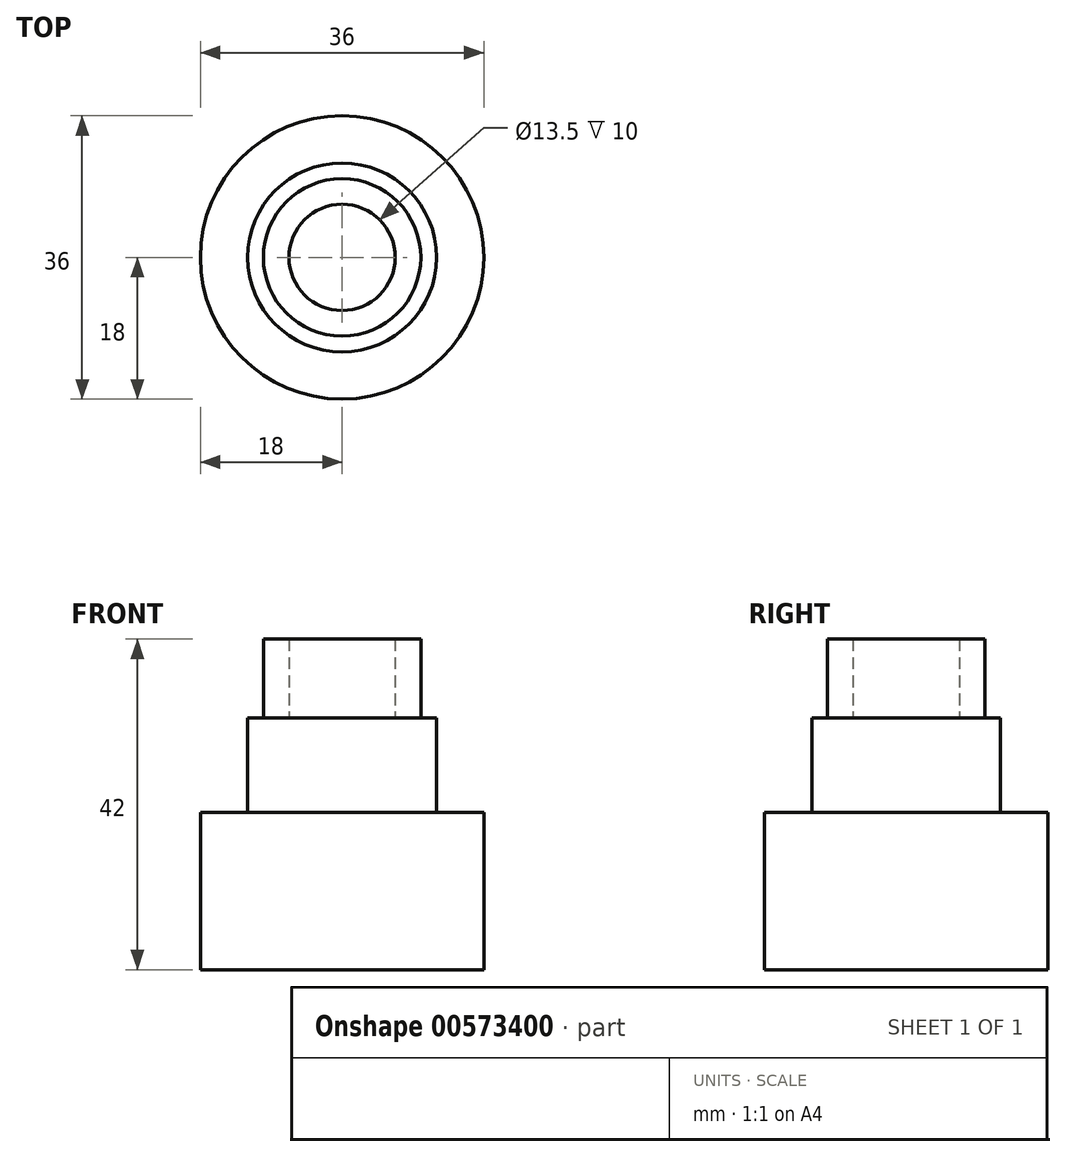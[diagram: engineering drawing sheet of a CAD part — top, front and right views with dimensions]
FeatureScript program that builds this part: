
annotation { "Feature Type Name" : "Feature", "Feature Type Description" : "" }
export const myFeature = defineFeature(function(context is Context, id is Id, definition is map)
    precondition{}
    {
        {
            var Q0;
            Q0=qCreatedBy(makeId("Top.planeOp"),FACE);
            var sketch = newSketch(context, id + "F0", { "sketchPlane" : qUnion([Q0])});
            skCircle(sketch, "E0", {"center": v(0, 0) * mm, "radius": 10 * mm});
            skCircle(sketch, "E1", {"center": v(0, 0) * mm, "radius": 12 * mm});
            skCircle(sketch, "E2", {"center": v(0, 0) * mm, "radius": 18 * mm});
            skCircle(sketch, "E3", {"center": v(0, 0) * mm, "radius": 6.75 * mm});
            skSolve(sketch);
        }
        {
            var Q0;
            Q0=makeQuery(id+"F0.imprint","IMPRINT",FACE,{"disambiguationData":[TD([[makeQuery(id+"F0.imprint","IMPRINT",EDGE,{"derivedFrom":sQuery(id+"F0.wireOp",EDGE,"E0")}),1.0]])]});
            extrude(context, id + "F1", {"entities" : qUnion([Q0]), "depth" : 42 * mm, "offsetDistance" : 25 * mm});
        }
        {
            var Q0;
            Q0=makeQuery(id+"F0.imprint","IMPRINT",FACE,{"disambiguationData":[TD([[makeQuery(id+"F0.imprint","IMPRINT",EDGE,{"derivedFrom":sQuery(id+"F0.wireOp",EDGE,"E0")}),-1.0]])]});
            var Q1;
            Q1=makeQuery(id+"F0.imprint","IMPRINT",FACE,{"disambiguationData":[TD([[makeQuery(id+"F0.imprint","IMPRINT",EDGE,{"derivedFrom":sQuery(id+"F0.wireOp",EDGE,"E3")}),1.0]])]});
            extrude(context, id + "F2", {"entities" : qUnion([Q0, Q1]), "operationType" : NewBodyOperationType.ADD, "depth" : 32 * mm, "offsetDistance" : 25 * mm});
        }
        {
            var Q0;
            Q0=makeQuery(id+"F0.imprint","IMPRINT",FACE,{"disambiguationData":[TD([[makeQuery(id+"F0.imprint","IMPRINT",EDGE,{"derivedFrom":sQuery(id+"F0.wireOp",EDGE,"E1")}),-1.0]])]});
            extrude(context, id + "F3", {"entities" : qUnion([Q0]), "operationType" : NewBodyOperationType.ADD, "depth" : 20 * mm, "offsetDistance" : 25 * mm});
        }
    });
